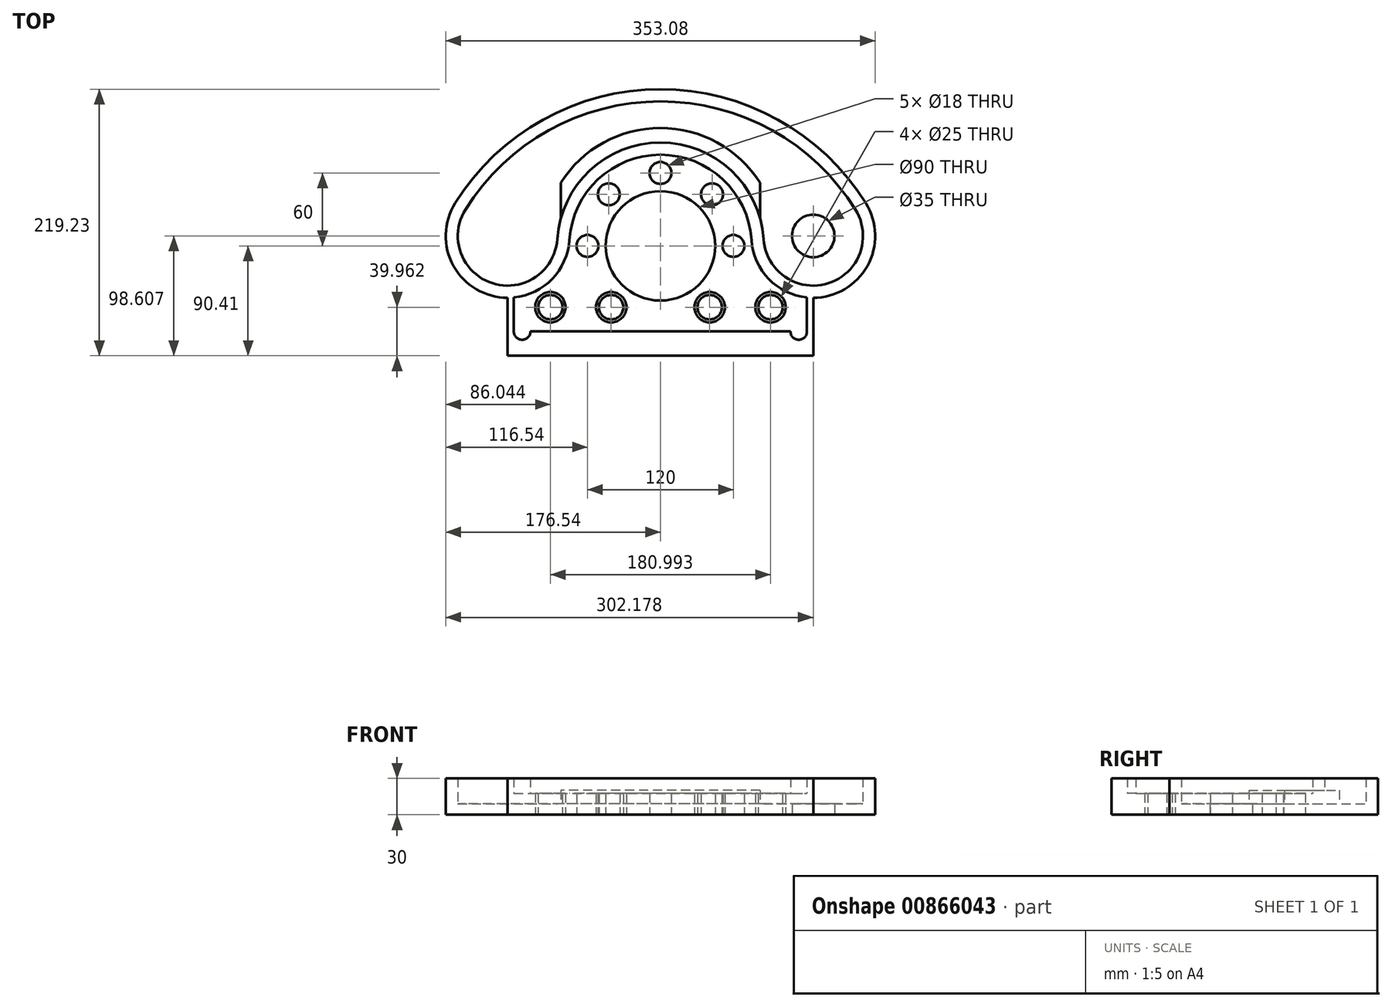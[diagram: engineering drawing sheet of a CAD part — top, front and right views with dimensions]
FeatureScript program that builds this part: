
annotation { "Feature Type Name" : "Feature", "Feature Type Description" : "" }
export const myFeature = defineFeature(function(context is Context, id is Id, definition is map)
    precondition{}
    {
        {
            var Q0;
            Q0=qCreatedBy(makeId("Top.planeOp"),FACE);
            var sketch = newSketch(context, id + "F0", { "sketchPlane" : qUnion([Q0])});
            skCircle(sketch, "E0", {"center": v(0, 0) * mm, "radius": 45 * mm});
            skArc(sketch, "E1", {"start": v(74.84, 4.88) * mm, "mid": v(0, 75) * mm, "end": v(-74.84, 4.88) * mm});
            skArc(sketch, "E2", {"start": v(84.82, 5.53) * mm, "mid": v(0, 85) * mm, "end": v(-84.82, 5.53) * mm});
            skLineSegment(sketch, "E3", {"start": v(-125.64, -32.7) * mm, "end": v(-125.64, -90.4) * mm});
            skLineSegment(sketch, "E4", {"start": v(-125.64, -90.4) * mm, "end": v(0, -90.4) * mm});
            skArc(sketch, "E5", {"start": v(-125.64, -32.7) * mm, "mid": v(-97.67, -21.65) * mm, "end": v(-84.82, 5.53) * mm});
            skArc(sketch, "E6", {"start": v(-120.5, -42.45) * mm, "mid": v(-89, -27.14) * mm, "end": v(-74.84, 4.88) * mm});
            skLineSegment(sketch, "E7", {"start": v(-120.5, -42.45) * mm, "end": v(-120.5, -70.4) * mm});
            skArc(sketch, "E8", {"start": v(-120.5, -70.4) * mm, "mid": v(-113.7, -77.21) * mm, "end": v(-106.9, -70.4) * mm});
            skLineSegment(sketch, "E9", {"start": v(-106.9, -70.4) * mm, "end": v(0, -70.4) * mm});
            skArc(sketch, "E10.MirrorCS", {"start": v(125.64, -32.7) * mm, "mid": v(97.67, -21.65) * mm, "end": v(84.82, 5.53) * mm});
            skArc(sketch, "E11.MirrorCS", {"start": v(120.5, -42.45) * mm, "mid": v(89, -27.14) * mm, "end": v(74.84, 4.88) * mm});
            skLineSegment(sketch, "E12.MirrorCS", {"start": v(125.64, -32.7) * mm, "end": v(125.64, -90.4) * mm});
            skLineSegment(sketch, "E13.MirrorCS", {"start": v(120.5, -42.45) * mm, "end": v(120.5, -70.4) * mm});
            skArc(sketch, "E14.MirrorCS", {"start": v(120.5, -70.4) * mm, "mid": v(113.7, -77.21) * mm, "end": v(106.9, -70.4) * mm});
            skLineSegment(sketch, "E15.MirrorCS", {"start": v(106.9, -70.4) * mm, "end": v(0, -70.4) * mm});
            skLineSegment(sketch, "E16.MirrorCS", {"start": v(125.64, -90.4) * mm, "end": v(0, -90.4) * mm});
            skPoint(sketch, "E17.orphan", {"position": v(125.64, -42.7) * mm});
            skPoint(sketch, "E18.orphan", {"position": v(-125.64, -42.7) * mm});
            skSolve(sketch);
        }
        {
            var Q0;
            {var subQ2=sQuery(id+"F0.wireOp",EDGE,"E1");Q0=makeQuery(id+"F0.imprint","IMPRINT",FACE,{"disambiguationData":[TD([[makeQuery(id+"F0.imprint","IMPRINT",EDGE,{"derivedFrom":subQ2}),-1.0]])]});}
            var Q1;
            Q1=makeQuery(id+"F0.imprint","IMPRINT",FACE,{"disambiguationData":[TD([[makeQuery(id+"F0.imprint","IMPRINT",EDGE,{"derivedFrom":sQuery(id+"F0.wireOp",EDGE,"E0")}),-1.0]])]});
            extrude(context, id + "F1", {"entities" : qUnion([Q0, Q1]), "depth" : 17.5 * mm, "offsetDistance" : 25 * mm});
        }
        {
            var Q0;
            {var subQ2=sQuery(id+"F0.wireOp",EDGE,"E1");Q0=makeQuery(id+"F0.imprint","IMPRINT",FACE,{"disambiguationData":[TD([[makeQuery(id+"F0.imprint","IMPRINT",EDGE,{"derivedFrom":subQ2}),-1.0]])]});}
            extrude(context, id + "F2", {"entities" : qUnion([Q0]), "operationType" : NewBodyOperationType.ADD, "depth" : 30 * mm, "offsetDistance" : 25 * mm});
        }
        {
            var Q0;
            Q0=qCreatedBy(makeId("Top.planeOp"),FACE);
            var sketch = newSketch(context, id + "F3", { "sketchPlane" : qUnion([Q0])});
            skArc(sketch, "E19", {"start": v(81.93, 51.92) * mm, "mid": v(0, 97) * mm, "end": v(-81.93, 51.92) * mm});
            skLineSegment(sketch, "E20", {"start": v(-81.93, 22.63) * mm, "end": v(-81.93, 51.92) * mm});
            skArc(sketch, "E21.0", {"start": v(84.82, 5.53) * mm, "mid": v(0, 85) * mm, "end": v(-84.82, 5.53) * mm});
            skLineSegment(sketch, "E22.MirrorCS", {"start": v(81.93, 22.63) * mm, "end": v(81.93, 51.92) * mm});
            skPoint(sketch, "E23.orphan", {"position": v(-81.93, 0) * mm});
            skPoint(sketch, "E24.orphan", {"position": v(81.93, 0) * mm});
            skSolve(sketch);
        }
        {
            var Q0;
            Q0=makeQuery(id+"F3.imprint","IMPRINT",FACE,{"disambiguationData":[TD([[makeQuery(id+"F3.imprint","IMPRINT",EDGE,{"derivedFrom":sQuery(id+"F3.wireOp",EDGE,"E19")}),1.0]])]});
            extrude(context, id + "F4", {"entities" : qUnion([Q0]), "operationType" : NewBodyOperationType.ADD, "depth" : 20 * mm, "offsetDistance" : 25 * mm});
        }
        {
            var Q0;
            Q0=qCreatedBy(makeId("Top.planeOp"),FACE);
            var sketch = newSketch(context, id + "F5", { "sketchPlane" : qUnion([Q0])});
            skPoint(sketch, "E25.0", {"position": v(125.64, 8.2) * mm});
            skPoint(sketch, "E26.0", {"position": v(125.64, -32.7) * mm});
            skArc(sketch, "E27", {"start": v(125.64, -32.7) * mm, "mid": v(161.4, -11.65) * mm, "end": v(160.35, 29.84) * mm});
            skArc(sketch, "E28", {"start": v(160.35, 29.84) * mm, "mid": v(91.69, 95.08) * mm, "end": v(0, 118.82) * mm});
            skArc(sketch, "E29.MirrorCS", {"start": v(-160.35, 29.84) * mm, "mid": v(-91.69, 95.08) * mm, "end": v(0, 118.82) * mm});
            skArc(sketch, "E30.MirrorC", {"start": v(-125.64, -32.7) * mm, "mid": v(-161.4, -11.65) * mm, "end": v(-160.35, 29.84) * mm});
            skArc(sketch, "E31.0", {"start": v(-125.64, -32.7) * mm, "mid": v(-97.67, -21.65) * mm, "end": v(-84.82, 5.53) * mm});
            skPoint(sketch, "E32.0", {"position": v(-81.93, 37.27) * mm});
            skArc(sketch, "E33.0", {"start": v(81.93, 51.92) * mm, "mid": v(0, 97) * mm, "end": v(-81.93, 51.92) * mm});
            skPoint(sketch, "E34.0", {"position": v(81.93, 37.27) * mm});
            skPoint(sketch, "E35.0", {"position": v(97.67, -21.65) * mm});
            skPoint(sketch, "E36.0", {"position": v(84.82, 5.53) * mm});
            skArc(sketch, "E37.0", {"start": v(125.64, -32.7) * mm, "mid": v(97.67, -21.65) * mm, "end": v(84.82, 5.53) * mm});
            skPoint(sketch, "E38.0", {"position": v(81.93, 22.63) * mm});
            skPoint(sketch, "E39.0", {"position": v(83.81, 14.15) * mm});
            skArc(sketch, "E40.0", {"start": v(84.82, 5.53) * mm, "mid": v(83.81, 14.15) * mm, "end": v(81.93, 22.63) * mm});
            skLineSegment(sketch, "E41.0", {"start": v(81.93, 22.63) * mm, "end": v(81.93, 51.92) * mm});
            skLineSegment(sketch, "E42.0", {"start": v(-81.93, 22.63) * mm, "end": v(-81.93, 51.92) * mm});
            skPoint(sketch, "E43.0", {"position": v(-81.93, 22.63) * mm});
            skPoint(sketch, "E44.0.end.orphan", {"position": v(-84.82, 5.53) * mm});
            skArc(sketch, "E45.0", {"start": v(-81.93, 22.63) * mm, "mid": v(-83.81, 14.15) * mm, "end": v(-84.82, 5.53) * mm});
            skSolve(sketch);
        }
        {
            var Q0;
            Q0=qSketchRegion(id+"F5",true);
            extrude(context, id + "F6", {"entities" : qUnion([Q0]), "operationType" : NewBodyOperationType.ADD, "depth" : 9 * mm, "offsetDistance" : 25 * mm});
        }
        {
            var Q0;
            Q0=makeQuery(id+"F0.imprint","IMPRINT",FACE,{"disambiguationData":[TD([[makeQuery(id+"F0.imprint","IMPRINT",EDGE,{"derivedFrom":sQuery(id+"F0.wireOp",EDGE,"E0")}),1.0]])]});
            var sketch = newSketch(context, id + "F7", { "sketchPlane" : qUnion([Q0])});
            skPoint(sketch, "E46.0", {"position": v(125.64, -90.4) * mm});
            skPoint(sketch, "E47.0", {"position": v(120.5, -42.45) * mm});
            skPoint(sketch, "E48.0", {"position": v(125.64, 8.2) * mm});
            skPoint(sketch, "E49.0", {"position": v(-120.5, -42.45) * mm});
            skPoint(sketch, "E50.0", {"position": v(-125.64, 8.2) * mm});
            skPoint(sketch, "E51.0", {"position": v(-125.64, -90.4) * mm});
            skPoint(sketch, "E52.0", {"position": v(0, -70.15) * mm});
            skArc(sketch, "E53", {"start": v(125.64, -42.7) * mm, "mid": v(170.15, -16.5) * mm, "end": v(168.83, 35.13) * mm});
            skArc(sketch, "E54", {"start": v(-168.83, 35.13) * mm, "mid": v(-170.15, -16.5) * mm, "end": v(-125.64, -42.7) * mm});
            skArc(sketch, "E55", {"start": v(168.83, 35.13) * mm, "mid": v(0, 128.82) * mm, "end": v(-168.83, 35.13) * mm});
            skPoint(sketch, "E56.0", {"position": v(-125.64, -32.7) * mm});
            skPoint(sketch, "E57.0", {"position": v(-125.64, -42.7) * mm});
            skPoint(sketch, "E58.0", {"position": v(125.64, -32.7) * mm});
            skPoint(sketch, "E59.0", {"position": v(125.64, -42.7) * mm});
            skLineSegment(sketch, "E60", {"start": v(125.64, -42.7) * mm, "end": v(125.64, -32.7) * mm});
            skLineSegment(sketch, "E61", {"start": v(-125.64, -42.7) * mm, "end": v(-125.64, -32.7) * mm});
            skArc(sketch, "E62.2", {"start": v(125.64, -32.7) * mm, "mid": v(161.4, -11.65) * mm, "end": v(160.35, 29.84) * mm});
            skArc(sketch, "E62.3", {"start": v(160.35, 29.84) * mm, "mid": v(91.69, 95.08) * mm, "end": v(0, 118.82) * mm});
            skArc(sketch, "E62.4", {"start": v(-160.35, 29.84) * mm, "mid": v(-91.69, 95.08) * mm, "end": v(0, 118.82) * mm});
            skArc(sketch, "E62.5", {"start": v(-125.64, -32.7) * mm, "mid": v(-161.4, -11.65) * mm, "end": v(-160.35, 29.84) * mm});
            skPoint(sketch, "E62.9", {"position": v(-161.4, -11.65) * mm});
            skSolve(sketch);
        }
        {
            var Q0;
            Q0=makeQuery(id+"F7.imprint","IMPRINT",FACE,{"disambiguationData":[TD([[makeQuery(id+"F7.imprint","IMPRINT",EDGE,{"derivedFrom":sQuery(id+"F7.wireOp",EDGE,"E53")}),1.0]])]});
            extrude(context, id + "F8", {"entities" : qUnion([Q0]), "operationType" : NewBodyOperationType.ADD, "depth" : 25 * mm, "offsetDistance" : 25 * mm});
        }
        {
            var Q0;
            Q0=makeQuery(id+"F0.imprint","IMPRINT",FACE,{"disambiguationData":[TD([[makeQuery(id+"F0.imprint","IMPRINT",EDGE,{"derivedFrom":sQuery(id+"F0.wireOp",EDGE,"E0")}),1.0]])]});
            var sketch = newSketch(context, id + "F9", { "sketchPlane" : qUnion([Q0])});
            skPoint(sketch, "E63.0", {"position": v(125.64, 8.2) * mm});
            skPoint(sketch, "E64.0", {"position": v(-125.64, 8.2) * mm});
            skCircle(sketch, "E65", {"center": v(125.64, 8.2) * mm, "radius": 17.5 * mm});
            skPoint(sketch, "E66.0", {"position": v(120.5, -56.43) * mm});
            skPoint(sketch, "E67.0", {"position": v(-120.5, -56.43) * mm});
            skPoint(sketch, "E68.0", {"position": v(-120.5, -42.45) * mm});
            skPoint(sketch, "E69.0", {"position": v(120.5, -42.45) * mm});
            skLineSegment(sketch, "E70", {"start": v(-120.5, -42.45) * mm, "end": v(-120.5, -50.45) * mm});
            skLineSegment(sketch, "E71", {"start": v(-120.5, -50.45) * mm, "end": v(120.5, -50.45) * mm});
            skLineSegment(sketch, "E72", {"start": v(-120.5, -50.45) * mm, "end": v(-90.5, -50.45) * mm});
            skLineSegment(sketch, "E73", {"start": v(-90.5, -50.45) * mm, "end": v(9.5, -50.45) * mm});
            skLineSegment(sketch, "E74", {"start": v(-90.5, -50.45) * mm, "end": v(-40.5, -50.45) * mm});
            skLineSegment(sketch, "E75", {"start": v(120.5, -50.45) * mm, "end": v(90.5, -50.45) * mm});
            skLineSegment(sketch, "E76", {"start": v(90.5, -50.45) * mm, "end": v(40.5, -50.45) * mm});
            skCircle(sketch, "E77", {"center": v(-90.5, -50.45) * mm, "radius": 12.5 * mm});
            skCircle(sketch, "E78", {"center": v(-40.5, -50.45) * mm, "radius": 12.5 * mm});
            skCircle(sketch, "E79", {"center": v(40.5, -50.45) * mm, "radius": 12.5 * mm});
            skCircle(sketch, "E80", {"center": v(90.5, -50.45) * mm, "radius": 12.5 * mm});
            skCircle(sketch, "E81", {"center": v(-90.5, -50.45) * mm, "radius": 10 * mm});
            skCircle(sketch, "E82", {"center": v(-40.5, -50.45) * mm, "radius": 10 * mm});
            skCircle(sketch, "E83", {"center": v(40.5, -50.45) * mm, "radius": 10 * mm});
            skCircle(sketch, "E84", {"center": v(90.5, -50.45) * mm, "radius": 10 * mm});
            skSolve(sketch);
        }
        {
            var Q0;
            Q0=makeQuery(id+"F9.imprint","IMPRINT",FACE,{"disambiguationData":[TD([[makeQuery(id+"F9.imprint","IMPRINT",EDGE,{"derivedFrom":sQuery(id+"F9.wireOp",EDGE,"E65")}),1.0]])]});
            extrude(context, id + "F10", {"entities" : qUnion([Q0]), "operationType" : NewBodyOperationType.REMOVE, "depth" : 25 * mm, "offsetDistance" : 25 * mm});
        }
        {
            var Q0;
            Q0=makeQuery(id+"F0.imprint","IMPRINT",FACE,{"disambiguationData":[TD([[makeQuery(id+"F0.imprint","IMPRINT",EDGE,{"derivedFrom":sQuery(id+"F0.wireOp",EDGE,"E0")}),1.0]])]});
            var sketch = newSketch(context, id + "F11", { "sketchPlane" : qUnion([Q0])});
            skCircle(sketch, "E85.0", {"center": v(0, 0) * mm, "radius": 45 * mm});
            skLineSegment(sketch, "E86.0.0", {"start": v(-106.9, -70.4) * mm, "end": v(106.9, -70.4) * mm});
            skArc(sketch, "E86.0.1", {"start": v(106.9, -70.4) * mm, "mid": v(113.7, -77.21) * mm, "end": v(120.5, -70.4) * mm});
            skLineSegment(sketch, "E86.0.2", {"start": v(120.5, -70.4) * mm, "end": v(120.5, -42.45) * mm});
            skArc(sketch, "E86.0.3", {"start": v(120.5, -42.45) * mm, "mid": v(89, -27.14) * mm, "end": v(74.84, 4.88) * mm});
            skArc(sketch, "E86.0.4", {"start": v(-74.84, 4.88) * mm, "mid": v(0, 75) * mm, "end": v(74.84, 4.88) * mm});
            skArc(sketch, "E86.0.5", {"start": v(-74.84, 4.88) * mm, "mid": v(-89, -27.14) * mm, "end": v(-120.5, -42.45) * mm});
            skLineSegment(sketch, "E86.0.6", {"start": v(-120.5, -42.45) * mm, "end": v(-120.5, -70.4) * mm});
            skArc(sketch, "E86.0.7", {"start": v(-106.9, -70.4) * mm, "mid": v(-113.7, -77.21) * mm, "end": v(-120.5, -70.4) * mm});
            skLineSegment(sketch, "E87", {"start": v(0, 0) * mm, "end": v(0, 45) * mm});
            skLineSegment(sketch, "E88", {"start": v(0, 45) * mm, "end": v(0, 60) * mm});
            skLineSegment(sketch, "E89", {"start": v(0, 0) * mm, "end": v(45, 0) * mm});
            skLineSegment(sketch, "E90", {"start": v(0, 0) * mm, "end": v(-45, 0) * mm});
            skLineSegment(sketch, "E91", {"start": v(-45, 0) * mm, "end": v(-60, 0) * mm});
            skLineSegment(sketch, "E92", {"start": v(45, 0) * mm, "end": v(60, 0) * mm});
            skCircle(sketch, "E93", {"center": v(0, 60) * mm, "radius": 9 * mm});
            skCircle(sketch, "E94", {"center": v(60, 0) * mm, "radius": 9 * mm});
            skCircle(sketch, "E95", {"center": v(-60, 0) * mm, "radius": 9 * mm});
            skCircle(sketch, "E96", {"center": v(42.43, 42.43) * mm, "radius": 9 * mm});
            skCircle(sketch, "E97", {"center": v(-42.43, 42.43) * mm, "radius": 9 * mm});
            skSolve(sketch);
        }
        {
            var Q0;
            Q0=makeQuery(id+"F11.imprint","IMPRINT",FACE,{"disambiguationData":[TD([[makeQuery(id+"F11.imprint","IMPRINT",EDGE,{"derivedFrom":sQuery(id+"F11.wireOp",EDGE,"E95")}),1.0]])]});
            var Q1;
            Q1=makeQuery(id+"F11.imprint","IMPRINT",FACE,{"disambiguationData":[TD([[makeQuery(id+"F11.imprint","IMPRINT",EDGE,{"derivedFrom":sQuery(id+"F11.wireOp",EDGE,"E97")}),1.0]])]});
            var Q2;
            Q2=makeQuery(id+"F11.imprint","IMPRINT",FACE,{"disambiguationData":[TD([[makeQuery(id+"F11.imprint","IMPRINT",EDGE,{"derivedFrom":sQuery(id+"F11.wireOp",EDGE,"E93")}),1.0]])]});
            var Q3;
            Q3=makeQuery(id+"F11.imprint","IMPRINT",FACE,{"disambiguationData":[TD([[makeQuery(id+"F11.imprint","IMPRINT",EDGE,{"derivedFrom":sQuery(id+"F11.wireOp",EDGE,"E96")}),1.0]])]});
            var Q4;
            Q4=makeQuery(id+"F11.imprint","IMPRINT",FACE,{"disambiguationData":[TD([[makeQuery(id+"F11.imprint","IMPRINT",EDGE,{"derivedFrom":sQuery(id+"F11.wireOp",EDGE,"E94")}),1.0]])]});
            var Q5;
            Q5=sQuery(id+"F11.wireOp",EDGE,"E97");
            var Q6;
            Q6=sQuery(id+"F11.wireOp",EDGE,"E93");
            var Q7;
            Q7=sQuery(id+"F11.wireOp",EDGE,"E96");
            var Q8;
            Q8=sQuery(id+"F11.wireOp",EDGE,"E94");
            var Q9;
            Q9=sQuery(id+"F11.wireOp",EDGE,"E95");
            extrude(context, id + "F12", {"entities" : qUnion([Q0, Q1, Q2, Q3, Q4]), "operationType" : NewBodyOperationType.REMOVE, "surfaceEntities" : qUnion([Q5, Q6, Q7, Q8, Q9]), "depth" : 25 * mm, "offsetDistance" : 25 * mm});
        }
        {
            var Q0;
            {var subQ0=sQuery(id+"F9.wireOp",EDGE,"E76");var subQ1=sQuery(id+"F9.wireOp",EDGE,"E75");var subQ2=makeQuery(id+"F9.imprint","INTERSECT",VERTEX,{"derivedFrom":[subQ1,subQ0]});Q0=makeQuery(id+"F9.imprint","IMPRINT",FACE,{"disambiguationData":[TD([[makeQuery(id+"F9.imprint","IMPRINT",EDGE,{"disambiguationData":[TD([[subQ2,1.0]])],"derivedFrom":subQ1}),1.0]])]});}
            var Q1;
            {var subQ0=sQuery(id+"F9.wireOp",EDGE,"E76");var subQ1=sQuery(id+"F9.wireOp",EDGE,"E75");var subQ2=makeQuery(id+"F9.imprint","INTERSECT",VERTEX,{"derivedFrom":[subQ1,subQ0]});Q1=makeQuery(id+"F9.imprint","IMPRINT",FACE,{"disambiguationData":[TD([[makeQuery(id+"F9.imprint","IMPRINT",EDGE,{"disambiguationData":[TD([[subQ2,1.0]])],"derivedFrom":subQ1}),-1.0]])]});}
            var Q2;
            {var subQ0=sQuery(id+"F9.wireOp",EDGE,"E76");var subQ1=sQuery(id+"F9.wireOp",EDGE,"E71");var subQ2=makeQuery(id+"F9.imprint","INTERSECT",VERTEX,{"derivedFrom":[subQ1,subQ0]});Q2=makeQuery(id+"F9.imprint","IMPRINT",FACE,{"disambiguationData":[TD([[makeQuery(id+"F9.imprint","IMPRINT",EDGE,{"disambiguationData":[TD([[subQ2,1.0]])],"derivedFrom":subQ1}),1.0]])]});}
            var Q3;
            {var subQ0=sQuery(id+"F9.wireOp",EDGE,"E76");var subQ1=sQuery(id+"F9.wireOp",EDGE,"E71");var subQ2=makeQuery(id+"F9.imprint","INTERSECT",VERTEX,{"derivedFrom":[subQ1,subQ0]});Q3=makeQuery(id+"F9.imprint","IMPRINT",FACE,{"disambiguationData":[TD([[makeQuery(id+"F9.imprint","IMPRINT",EDGE,{"disambiguationData":[TD([[subQ2,1.0]])],"derivedFrom":subQ1}),-1.0]])]});}
            var Q4;
            {var subQ0=sQuery(id+"F9.wireOp",EDGE,"E74");var subQ1=sQuery(id+"F9.wireOp",EDGE,"E73");var subQ2=makeQuery(id+"F9.imprint","INTERSECT",VERTEX,{"derivedFrom":[subQ1,subQ0]});Q4=makeQuery(id+"F9.imprint","IMPRINT",FACE,{"disambiguationData":[TD([[makeQuery(id+"F9.imprint","IMPRINT",EDGE,{"disambiguationData":[TD([[subQ2,-1.0]])],"derivedFrom":subQ1}),1.0]])]});}
            var Q5;
            {var subQ0=sQuery(id+"F9.wireOp",EDGE,"E74");var subQ1=sQuery(id+"F9.wireOp",EDGE,"E73");var subQ2=makeQuery(id+"F9.imprint","INTERSECT",VERTEX,{"derivedFrom":[subQ1,subQ0]});Q5=makeQuery(id+"F9.imprint","IMPRINT",FACE,{"disambiguationData":[TD([[makeQuery(id+"F9.imprint","IMPRINT",EDGE,{"disambiguationData":[TD([[subQ2,-1.0]])],"derivedFrom":subQ1}),-1.0]])]});}
            var Q6;
            {var subQ0=sQuery(id+"F9.wireOp",EDGE,"E74");var subQ1=sQuery(id+"F9.wireOp",EDGE,"E72");var subQ2=makeQuery(id+"F9.imprint","INTERSECT",VERTEX,{"derivedFrom":[subQ1,subQ0]});Q6=makeQuery(id+"F9.imprint","IMPRINT",FACE,{"disambiguationData":[TD([[makeQuery(id+"F9.imprint","IMPRINT",EDGE,{"disambiguationData":[TD([[subQ2,1.0]])],"derivedFrom":subQ1}),1.0]])]});}
            var Q7;
            {var subQ0=sQuery(id+"F9.wireOp",EDGE,"E74");var subQ1=sQuery(id+"F9.wireOp",EDGE,"E72");var subQ2=makeQuery(id+"F9.imprint","INTERSECT",VERTEX,{"derivedFrom":[subQ1,subQ0]});Q7=makeQuery(id+"F9.imprint","IMPRINT",FACE,{"disambiguationData":[TD([[makeQuery(id+"F9.imprint","IMPRINT",EDGE,{"disambiguationData":[TD([[subQ2,1.0]])],"derivedFrom":subQ1}),-1.0]])]});}
            var Q8;
            Q8=sQuery(id+"F9.wireOp",EDGE,"E84");
            var Q9;
            Q9=sQuery(id+"F9.wireOp",EDGE,"E83");
            var Q10;
            Q10=sQuery(id+"F9.wireOp",EDGE,"E82");
            var Q11;
            Q11=sQuery(id+"F9.wireOp",EDGE,"E81");
            extrude(context, id + "F13", {"entities" : qUnion([Q0, Q1, Q2, Q3, Q4, Q5, Q6, Q7]), "operationType" : NewBodyOperationType.REMOVE, "surfaceEntities" : qUnion([Q8, Q9, Q10, Q11]), "depth" : 25 * mm, "offsetDistance" : 25 * mm});
        }
        {
            var Q0;
            Q0 = qSketchRegion(id + "F7", true);
            var Q1;
            Q1=makeQuery(id+"F8.opExtrude","CAP_FACE",FACE,{"disambiguationData":[OSD([sQuery(id+"F7.wireOp",EDGE,"E53"),sQuery(id+"F7.wireOp",EDGE,"E54"),sQuery(id+"F7.wireOp",EDGE,"E55"),sQuery(id+"F7.wireOp",EDGE,"E60"),sQuery(id+"F7.wireOp",EDGE,"E61"),sQuery(id+"F7.wireOp",EDGE,"E62.2"),sQuery(id+"F7.wireOp",EDGE,"E62.3"),sQuery(id+"F7.wireOp",EDGE,"E62.4"),sQuery(id+"F7.wireOp",EDGE,"E62.5")])],"isStart":false});
            extrude(context, id + "F14", {"entities" : qUnion([Q0, Q1]), "operationType" : NewBodyOperationType.ADD, "depth" : 5 * mm, "offsetDistance" : 25 * mm});
        }
    });
